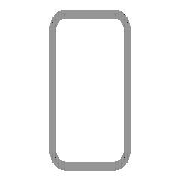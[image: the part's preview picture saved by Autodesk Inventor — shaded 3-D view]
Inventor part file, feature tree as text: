
AUTODESK INVENTOR PART (.ipt)
format: ipt  version: 2025 (Build 290162010, 162A)  size: 136,192 bytes
history: native  units: mm (DEFAULTED — no unit token found)
features: other x4, sketch x1, plane x1
ambient origin geometry x8: Origin, YZ Plane, XZ Plane, XY Plane, X Axis, Y Axis, Z Axis, Center Point
bodies: Solid1 (feature_tree), Body (feature_tree)
feature tree (6):
  parser-record x1  (decoder bookkeeping rows leaked as tree rows — omitted from the tree; the rows remain in map.json)
  other  "Driven Length"
  other  "Start plane"
  other  "End plane"
  sketch  "Sketch3"  dims[d3=600.0mm d4=0.0mm d7=6.0mm d9=40.0mm d11=60.0mm d12=3.0mm d13=-0.0mm d14=600.0mm d15=20.0mm d16=30.0mm d17=90.0deg d18=600.0mm]
  plane  "Work Plane3"
